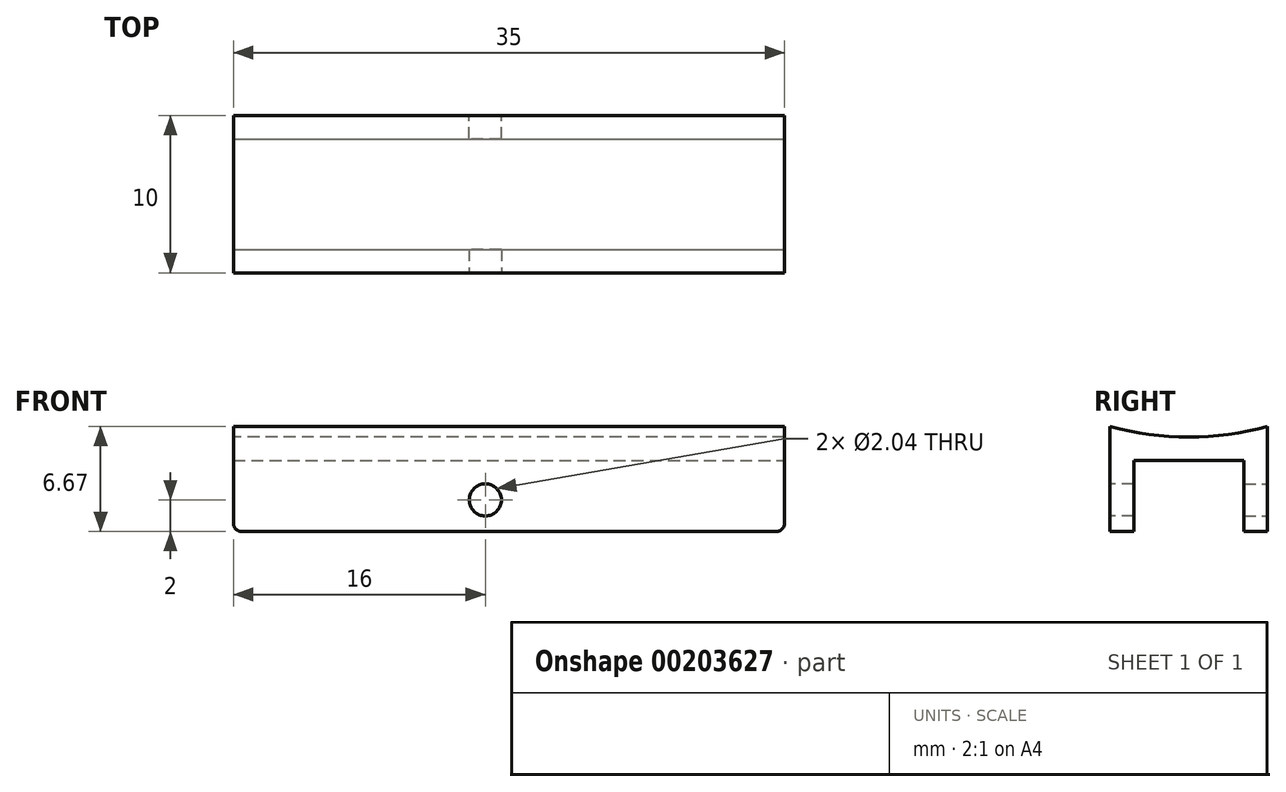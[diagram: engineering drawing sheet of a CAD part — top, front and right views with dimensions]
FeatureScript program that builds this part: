
annotation { "Feature Type Name" : "Feature", "Feature Type Description" : "" }
export const myFeature = defineFeature(function(context is Context, id is Id, definition is map)
    precondition{}
    {
        {
            var Q0;
            Q0=qCreatedBy(makeId("Top.planeOp"),FACE);
            var sketch = newSketch(context, id + "F0", { "sketchPlane" : qUnion([Q0])});
            skLineSegment(sketch, "E0.bottom", {"start": v(0, 0) * mm, "end": v(35, 0) * mm});
            skLineSegment(sketch, "E0.top", {"start": v(0, -5) * mm, "end": v(35, -5) * mm});
            skLineSegment(sketch, "E0.left", {"start": v(0, 0) * mm, "end": v(0, -5) * mm});
            skLineSegment(sketch, "E0.right", {"start": v(35, 0) * mm, "end": v(35, -5) * mm});
            skSolve(sketch);
        }
        {
            var Q0;
            Q0=makeQuery(id+"F0.imprint","IMPRINT",FACE,{"disambiguationData":[TD([[makeQuery(id+"F0.imprint","IMPRINT",EDGE,{"derivedFrom":sQuery(id+"F0.wireOp",EDGE,"E0.bottom")}),-1.0]])]});
            extrude(context, id + "F1", {"entities" : qUnion([Q0]), "oppositeDirection" : true, "depth" : 1.5 * mm});
        }
        {
            var Q0;
            Q0=makeQuery(id+"F1.opExtrude","CAP_FACE",FACE,{"disambiguationData":[OSD([sQuery(id+"F0.wireOp",EDGE,"E0.bottom"),sQuery(id+"F0.wireOp",EDGE,"E0.top"),sQuery(id+"F0.wireOp",EDGE,"E0.left"),sQuery(id+"F0.wireOp",EDGE,"E0.right")])],"isStart":false});
            var sketch = newSketch(context, id + "F2", { "sketchPlane" : qUnion([Q0])});
            skLineSegment(sketch, "E1.bottom", {"start": v(0, 5) * mm, "end": v(35, 5) * mm});
            skLineSegment(sketch, "E1.top", {"start": v(0, 3.5) * mm, "end": v(35, 3.5) * mm});
            skLineSegment(sketch, "E1.left", {"start": v(0, 5) * mm, "end": v(0, 3.5) * mm});
            skLineSegment(sketch, "E1.right", {"start": v(35, 5) * mm, "end": v(35, 3.5) * mm});
            skSolve(sketch);
        }
        {
            var Q0;
            Q0 = qSketchRegion(id + "F2", true);
            extrude(context, id + "F3", {"entities" : qUnion([Q0]), "operationType" : NewBodyOperationType.ADD, "depth" : 4.5 * mm});
        }
        {
            var Q0;
            Q0=makeQuery(id+"F3.boolean.opBoolean","MERGE",FACE,{"derivedFrom":[makeQuery(id+"F1.opExtrude","SWEPT_FACE",FACE,{"disambiguationData":[OSD([sQuery(id+"F0.wireOp",EDGE,"E0.top")])]}),makeQuery(id+"F3.opExtrude","SWEPT_FACE",FACE,{"disambiguationData":[OSD([sQuery(id+"F2.wireOp",EDGE,"E1.bottom")])]})]});
            var sketch = newSketch(context, id + "F4", { "sketchPlane" : qUnion([Q0])});
            skCircle(sketch, "E2", {"center": v(16, -4) * mm, "radius": 1.02 * mm});
            skSolve(sketch);
        }
        {
            var Q0;
            Q0 = qSketchRegion(id + "F4", true);
            extrude(context, id + "F5", {"entities" : qUnion([Q0]), "operationType" : NewBodyOperationType.REMOVE, "endBound" : BoundingType.THROUGH_ALL, "oppositeDirection" : true, "depth" : 25 * mm});
        }
        {
            var Q0;
            Q0=makeQuery(id+"F3.opExtrude","CAP_EDGE",EDGE,{"disambiguationData":[OSD([sQuery(id+"F2.wireOp",EDGE,"E1.right")])],"isStart":false});
            var Q1;
            Q1=makeQuery(id+"F3.opExtrude","CAP_EDGE",EDGE,{"disambiguationData":[OSD([sQuery(id+"F2.wireOp",EDGE,"E1.left")])],"isStart":false});
            fillet(context, id + "F6", {"entities" : qUnion([Q0, Q1]), "radius" : .5 * mm, "tangentPropagation" : true, "allowEdgeOverflow" : false});
        }
        {
            var Q0;
            Q0=makeQuery(id+"F1.opExtrude","SWEPT_BODY",BODY,{"disambiguationData":[OSD([sQuery(id+"F0.wireOp",EDGE,"E0.bottom"),sQuery(id+"F0.wireOp",EDGE,"E0.top"),sQuery(id+"F0.wireOp",EDGE,"E0.left"),sQuery(id+"F0.wireOp",EDGE,"E0.right")])]});
            var Q1;
            Q1=qCreatedBy(makeId("Front.planeOp"),FACE);
            mirror(context, id + "F7", {"operationType" : NewBodyOperationType.ADD, "entities" : qUnion([Q0]), "mirrorPlane" : qUnion([Q1])});
        }
        {
            var Q0;
            Q0=qCreatedBy(makeId("Right.planeOp"),FACE);
            var sketch = newSketch(context, id + "F8", { "sketchPlane" : qUnion([Q0])});
            skCircle(sketch, "E3", {"center": v(0, 19.05) * mm, "radius": 19.05 * mm});
            skLineSegment(sketch, "E4.0", {"start": v(5, 0) * mm, "end": v(-5, 0) * mm});
            skLineSegment(sketch, "E5", {"start": v(5, 0) * mm, "end": v(5, 0.67) * mm});
            skLineSegment(sketch, "E6", {"start": v(-5, 0) * mm, "end": v(-5, 0.67) * mm});
            skSolve(sketch);
        }
        {
            var Q0;
            {var subQ0=sQuery(id+"F8.wireOp",EDGE,"E6");Q0=makeQuery(id+"F8.imprint","IMPRINT",FACE,{"disambiguationData":[TD([[makeQuery(id+"F8.imprint","IMPRINT",EDGE,{"derivedFrom":subQ0}),-1.0]])]});}
            var Q1;
            {var subQ0=sQuery(id+"F8.wireOp",EDGE,"E5");Q1=makeQuery(id+"F8.imprint","IMPRINT",FACE,{"disambiguationData":[TD([[makeQuery(id+"F8.imprint","IMPRINT",EDGE,{"derivedFrom":subQ0}),1.0]])]});}
            var Q2;
            {var subQ0=makeQuery(id+"F3.boolean.opBoolean","MERGE",FACE,{"derivedFrom":[makeQuery(id+"F1.opExtrude","SWEPT_FACE",FACE,{"disambiguationData":[OSD([sQuery(id+"F0.wireOp",EDGE,"E0.right")])]}),makeQuery(id+"F3.opExtrude","SWEPT_FACE",FACE,{"disambiguationData":[OSD([sQuery(id+"F2.wireOp",EDGE,"E1.right")])]})]});Q2=makeQuery(id+"F7.boolean.opBoolean","MERGE",FACE,{"derivedFrom":[subQ0,makeQuery(id+"F7.opPattern","COPY",FACE,{"derivedFrom":subQ0,"instanceName":"1"})]});}
            extrude(context, id + "F9", {"entities" : qUnion([Q0, Q1]), "operationType" : NewBodyOperationType.ADD, "endBound" : BoundingType.UP_TO_SURFACE, "endBoundEntityFace" : qUnion([Q2]), "depth" : 25 * mm});
        }
    });
